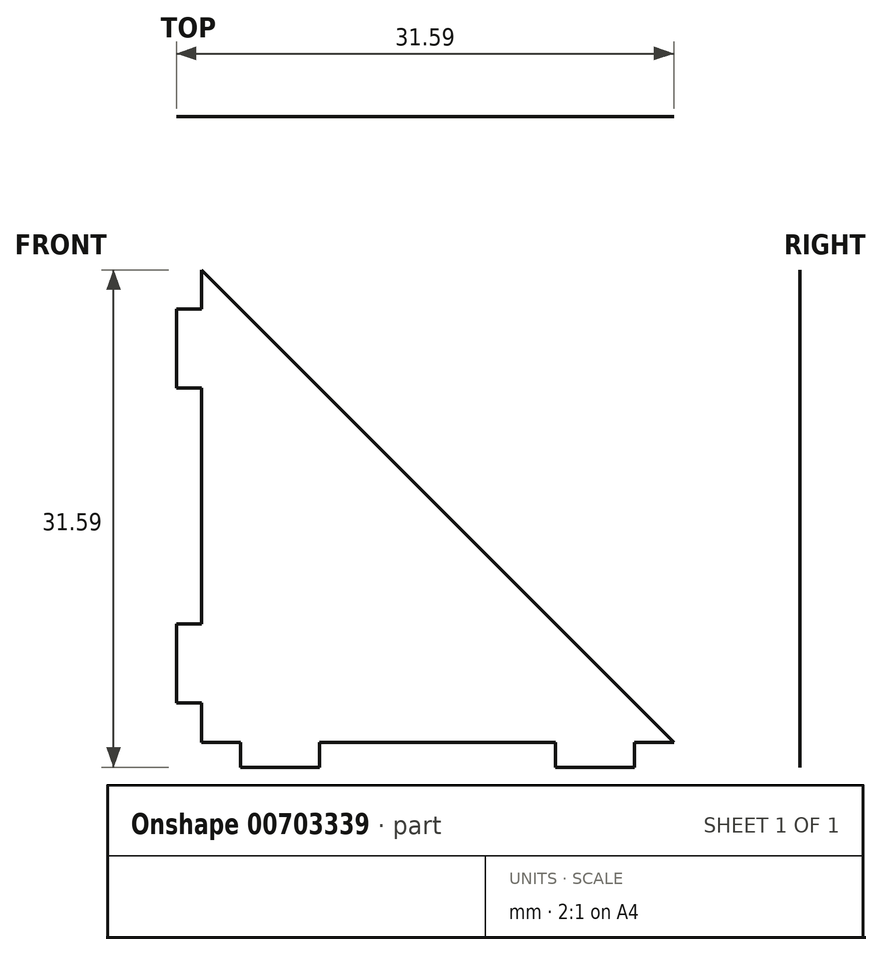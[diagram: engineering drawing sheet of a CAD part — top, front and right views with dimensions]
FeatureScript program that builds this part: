
annotation { "Feature Type Name" : "Feature", "Feature Type Description" : "" }
export const myFeature = defineFeature(function(context is Context, id is Id, definition is map)
    precondition{}
    {
        {
            var Q0;
            Q0=qCreatedBy(makeId("Front.planeOp"),FACE);
            var sketch = newSketch(context, id + "F0", { "sketchPlane" : qUnion([Q0])});
            skLineSegment(sketch, "E0", {"start": v(0, 0) * mm, "end": v(0, 33.17) * mm});
            skLineSegment(sketch, "E1", {"start": v(0, 33.17) * mm, "end": v(33.18, 0) * mm});
            skLineSegment(sketch, "E2", {"start": v(33.18, 0) * mm, "end": v(0, 0) * mm});
            skLineSegment(sketch, "E3", {"start": v(1.59, 31.59) * mm, "end": v(1.59, 29.09) * mm});
            skLineSegment(sketch, "E4", {"start": v(1.59, 29.09) * mm, "end": v(0, 29.09) * mm});
            skLineSegment(sketch, "E5", {"start": v(0, 24.09) * mm, "end": v(1.59, 24.09) * mm});
            skLineSegment(sketch, "E6", {"start": v(1.59, 24.09) * mm, "end": v(1.59, 9.09) * mm});
            skLineSegment(sketch, "E7", {"start": v(1.59, 9.09) * mm, "end": v(0, 9.09) * mm});
            skLineSegment(sketch, "E8", {"start": v(0, 4.09) * mm, "end": v(1.59, 4.09) * mm});
            skLineSegment(sketch, "E9", {"start": v(1.59, 4.09) * mm, "end": v(1.59, 1.59) * mm});
            skLineSegment(sketch, "E10", {"start": v(1.59, 1.59) * mm, "end": v(4.09, 1.59) * mm});
            skLineSegment(sketch, "E11", {"start": v(4.09, 1.59) * mm, "end": v(4.09, 0) * mm});
            skLineSegment(sketch, "E12", {"start": v(9.09, 0) * mm, "end": v(9.09, 1.59) * mm});
            skLineSegment(sketch, "E13", {"start": v(9.09, 1.59) * mm, "end": v(24.09, 1.59) * mm});
            skLineSegment(sketch, "E14", {"start": v(24.09, 1.59) * mm, "end": v(24.09, 0) * mm});
            skLineSegment(sketch, "E15", {"start": v(29.09, 0) * mm, "end": v(29.09, 1.59) * mm});
            skLineSegment(sketch, "E16", {"start": v(29.09, 1.59) * mm, "end": v(31.59, 1.59) * mm});
            skSolve(sketch);
        }
        {
            var Q0;
            {var subQ1=sQuery(id+"F0.wireOp",EDGE,"E3");Q0=makeQuery(id+"F0.imprint","IMPRINT",FACE,{"disambiguationData":[TD([[makeQuery(id+"F0.imprint","IMPRINT",EDGE,{"derivedFrom":subQ1}),1.0]])]});}
            extrude(context, id + "F1", {"entities" : qUnion([Q0]), "depth" : 1 / 406.4 * mm, "offsetDistance" : 25 * mm});
        }
    });
